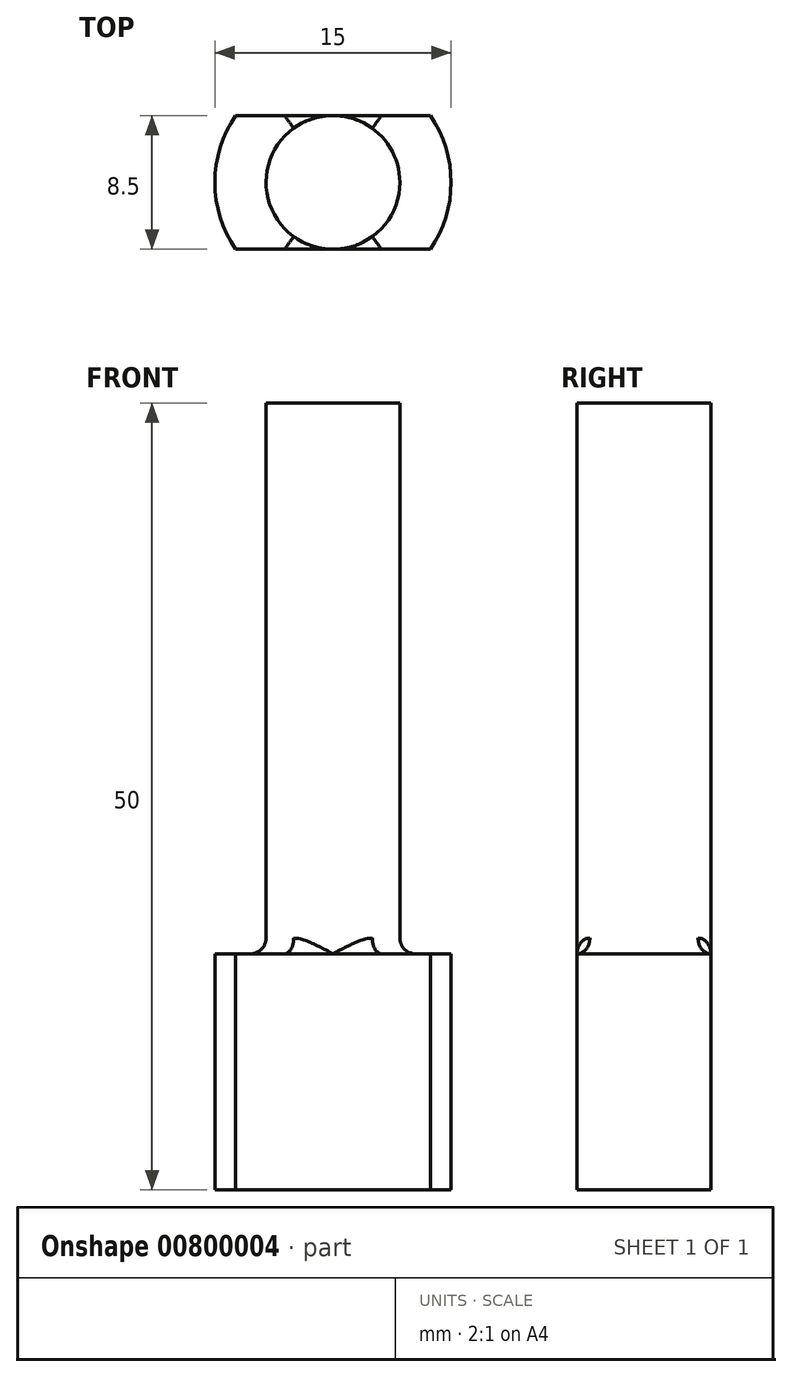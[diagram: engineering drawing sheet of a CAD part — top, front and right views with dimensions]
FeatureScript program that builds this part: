
annotation { "Feature Type Name" : "Feature", "Feature Type Description" : "" }
export const myFeature = defineFeature(function(context is Context, id is Id, definition is map)
    precondition{}
    {
        {
            var Q0;
            Q0=qCreatedBy(makeId("Top.planeOp"),FACE);
            var sketch = newSketch(context, id + "F0", { "sketchPlane" : qUnion([Q0])});
            skCircle(sketch, "E0", {"center": v(0, 0) * mm, "radius": 4.25 * mm});
            skSolve(sketch);
        }
        {
            var Q0;
            Q0=makeQuery(id+"F0.imprint","IMPRINT",FACE,{"disambiguationData":[TD([[makeQuery(id+"F0.imprint","IMPRINT",EDGE,{"derivedFrom":sQuery(id+"F0.wireOp",EDGE,"E0")}),1.0]])]});
            extrude(context, id + "F1", {"entities" : qUnion([Q0]), "depth" : 35 * mm, "offsetDistance" : 25 * mm});
        }
        {
            var Q0;
            Q0=qCreatedBy(makeId("Top.planeOp"),FACE);
            var sketch = newSketch(context, id + "F2", { "sketchPlane" : qUnion([Q0])});
            skCircle(sketch, "E1", {"center": v(0, 0) * mm, "radius": 7.5 * mm});
            skLineSegment(sketch, "E2", {"start": v(6.18, -4.25) * mm, "end": v(-6.18, -4.25) * mm});
            skLineSegment(sketch, "E3.MirrorCS", {"start": v(6.18, 4.25) * mm, "end": v(-6.18, 4.25) * mm});
            skSolve(sketch);
        }
        {
            var Q0;
            Q0=makeQuery(id+"F2.imprint","IMPRINT",FACE,{"disambiguationData":[TD([[makeQuery(id+"F2.imprint","IMPRINT",EDGE,{"derivedFrom":sQuery(id+"F2.wireOp",EDGE,"E1")}),1.0]])]});
            extrude(context, id + "F3", {"entities" : qUnion([Q0]), "operationType" : NewBodyOperationType.ADD, "oppositeDirection" : true, "depth" : 15 * mm, "offsetDistance" : 25 * mm});
        }
        {
            var Q0;
            Q0=makeQuery(id+"F3.boolean.opBoolean","SPLIT",EDGE,{"disambiguationData":[OD(1.0)],"derivedFrom":makeQuery(id+"F1.opExtrude","CAP_EDGE",EDGE,{"disambiguationData":[OSD([sQuery(id+"F0.wireOp",EDGE,"E0")])],"isStart":true})});
            var Q1;
            Q1=makeQuery(id+"F3.boolean.opBoolean","SPLIT",EDGE,{"disambiguationData":[OD(0.0)],"derivedFrom":makeQuery(id+"F1.opExtrude","CAP_EDGE",EDGE,{"disambiguationData":[OSD([sQuery(id+"F0.wireOp",EDGE,"E0")])],"isStart":true})});
            fillet(context, id + "F4", {"entities" : qUnion([Q0, Q1]), "radius" : 1 * mm, "tangentPropagation" : true, "allowEdgeOverflow" : false});
        }
    });
